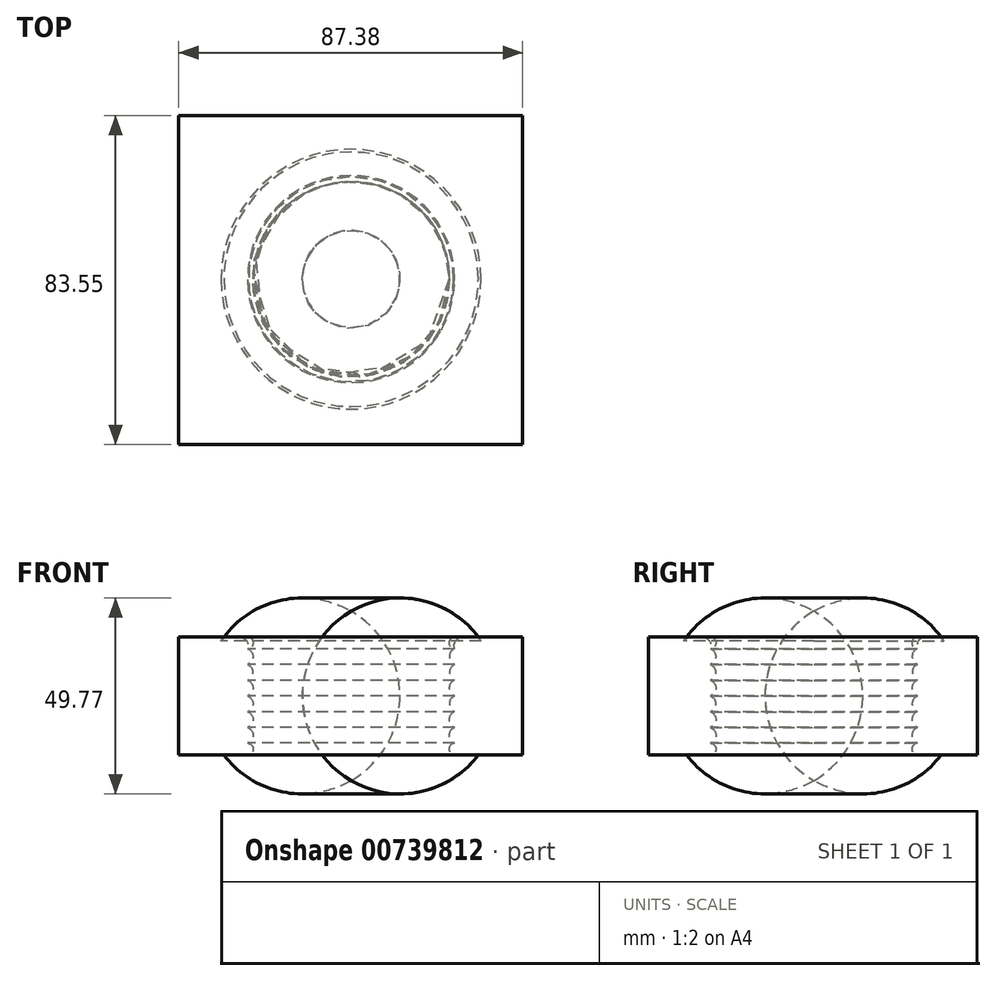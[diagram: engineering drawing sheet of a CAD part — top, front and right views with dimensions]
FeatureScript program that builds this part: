
annotation { "Feature Type Name" : "Feature", "Feature Type Description" : "" }
export const myFeature = defineFeature(function(context is Context, id is Id, definition is map)
    precondition{}
    {
        {
            var Q0;
            Q0=qCreatedBy(makeId("Top.planeOp"),FACE);
            cPlane(context, id + "F0", {"entities" : qUnion([Q0]), "cplaneType" : CPlaneType.OFFSET, "offset" : 30 * mm, "width" : 150 * mm, "height" : 150 * mm});
        }
        {
            var Q0;
            Q0=qCreatedBy(id+"F0.planeOp",FACE);
            var sketch = newSketch(context, id + "F1", { "sketchPlane" : qUnion([Q0])});
            skCircle(sketch, "E0", {"center": v(0, 0) * mm, "radius": 26 * mm});
            skCircle(sketch, "E1", {"center": v(0, 0) * mm, "radius": 32.5 * mm});
            skSolve(sketch);
        }
        {
            var Q0;
            Q0=qCreatedBy(makeId("Front.planeOp"),FACE);
            var sketch = newSketch(context, id + "F2", { "sketchPlane" : qUnion([Q0])});
            skArc(sketch, "E2", {"start": v(32.33, 0) * mm, "mid": v(37.35, 15) * mm, "end": v(32.32, 30) * mm});
            skLineSegment(sketch, "E3", {"start": v(12.47, 15) * mm, "end": v(50.15, 15) * mm, "construction": true});
            skLineSegment(sketch, "E4", {"start": v(12.47, 15) * mm, "end": v(12.47, 19) * mm, "construction": true});
            skLineSegment(sketch, "E5", {"start": v(12.47, 19) * mm, "end": v(49.8, 19) * mm, "construction": true});
            skLineSegment(sketch, "E6", {"start": v(49.8, 19) * mm, "end": v(49.8, 23) * mm, "construction": true});
            skLineSegment(sketch, "E7", {"start": v(49.8, 23) * mm, "end": v(12.47, 23) * mm, "construction": true});
            skLineSegment(sketch, "E8", {"start": v(12.47, 23) * mm, "end": v(12.47, 27) * mm, "construction": true});
            skLineSegment(sketch, "E9", {"start": v(12.47, 27) * mm, "end": v(49.98, 27) * mm, "construction": true});
            skLineSegment(sketch, "E10", {"start": v(49.98, 27) * mm, "end": v(49.98, 30) * mm, "construction": true});
            skLineSegment(sketch, "E11", {"start": v(50.15, 15) * mm, "end": v(50.15, 11) * mm, "construction": true});
            skLineSegment(sketch, "E12", {"start": v(50.15, 11) * mm, "end": v(12.79, 11) * mm, "construction": true});
            skLineSegment(sketch, "E13", {"start": v(12.79, 11) * mm, "end": v(12.79, 7) * mm, "construction": true});
            skLineSegment(sketch, "E14", {"start": v(12.79, 7) * mm, "end": v(50.15, 7) * mm, "construction": true});
            skLineSegment(sketch, "E15", {"start": v(50.15, 7) * mm, "end": v(50.15, 3) * mm, "construction": true});
            skLineSegment(sketch, "E16", {"start": v(50.15, 3) * mm, "end": v(13.06, 3) * mm, "construction": true});
            skLineSegment(sketch, "E17", {"start": v(13.06, 3) * mm, "end": v(13.06, 0) * mm, "construction": true});
            skLineSegment(sketch, "E18", {"start": v(13.06, 0) * mm, "end": v(50.15, 0) * mm, "construction": true});
            skArc(sketch, "E19", {"start": v(26, 29.95) * mm, "mid": v(24.87, 28.34) * mm, "end": v(26.32, 27) * mm});
            skArc(sketch, "E20", {"start": v(26.32, 27) * mm, "mid": v(24.95, 25) * mm, "end": v(26.32, 23) * mm});
            skArc(sketch, "E21", {"start": v(26.32, 23) * mm, "mid": v(24.99, 21) * mm, "end": v(26.32, 19) * mm});
            skArc(sketch, "E22", {"start": v(26.32, 19) * mm, "mid": v(24.91, 17) * mm, "end": v(26.32, 15) * mm});
            skArc(sketch, "E23", {"start": v(26.32, 15) * mm, "mid": v(24.95, 13) * mm, "end": v(26.32, 11) * mm});
            skArc(sketch, "E24", {"start": v(26.32, 11) * mm, "mid": v(24.9, 9) * mm, "end": v(26.32, 7) * mm});
            skArc(sketch, "E25", {"start": v(26.32, 7) * mm, "mid": v(24.9, 5) * mm, "end": v(26.32, 3) * mm});
            skArc(sketch, "E26", {"start": v(26.32, 3) * mm, "mid": v(24.9, 1.5) * mm, "end": v(26.32, 0) * mm});
            skLineSegment(sketch, "E27", {"start": v(26, 29.95) * mm, "end": v(32.32, 30) * mm});
            skLineSegment(sketch, "E28", {"start": v(26.32, 0) * mm, "end": v(32.33, 0) * mm});
            skLineSegment(sketch, "E29", {"start": v(25, 30.36) * mm, "end": v(24.9, -1.2) * mm, "construction": true});
            skPoint(sketch, "E29.endSnap0", {"position": v(24.9, 1.5) * mm});
            skSolve(sketch);
        }
        {
            var Q0;
            Q0=makeQuery(id+"F2.imprint","IMPRINT",FACE,{"disambiguationData":[TD([[makeQuery(id+"F2.imprint","IMPRINT",EDGE,{"derivedFrom":sQuery(id+"F2.wireOp",EDGE,"E2")}),1.0]])]});
            var Q1;
            Q1=sQuery(id+"F2.wireOp",EDGE,"E22");
            var Q2;
            Q2=sQuery(id+"F2.wireOp",EDGE,"E21");
            var Q3;
            Q3=sQuery(id+"F2.wireOp",EDGE,"E20");
            var Q4;
            Q4=sQuery(id+"F2.wireOp",EDGE,"E27");
            var Q5;
            Q5=sQuery(id+"F2.wireOp",EDGE,"E19");
            var Q6;
            Q6=sQuery(id+"F2.wireOp",EDGE,"E2");
            var Q7;
            Q7=sQuery(id+"F2.wireOp",EDGE,"E23");
            var Q8;
            Q8=sQuery(id+"F2.wireOp",EDGE,"E24");
            var Q9;
            Q9=sQuery(id+"F2.wireOp",EDGE,"E25");
            var Q10;
            Q10=sQuery(id+"F2.wireOp",EDGE,"E26");
            var Q11;
            Q11=sQuery(id+"F2.wireOp",EDGE,"E28");
            var Q12;
            Q12=sQuery(id+"F1.wireOp",EDGE,"E0");
            sweep(context, id + "F3", {"bodyType" : ExtendedToolBodyType.SURFACE, "profiles" : qUnion([Q0]), "surfaceProfiles" : qUnion([Q1, Q2, Q3, Q4, Q5, Q6, Q7, Q8, Q9, Q10, Q11]), "path" : qUnion([Q12])});
        }
        {
            var Q0;
            Q0=makeQuery(id+"F3.opSweep","SWEPT_FACE",FACE,{"disambiguationData":[OSD([sQuery(id+"F1.wireOp",EDGE,"E0"),sQuery(id+"F2.wireOp",EDGE,"E27")])]});
            fillet(context, id + "F4", {"entities" : qUnion([Q0]), "radius" : 2 * mm, "tangentPropagation" : true, "allowEdgeOverflow" : false});
        }
        {
            var Q0;
            Q0=qCreatedBy(id+"F0.planeOp",FACE);
            var sketch = newSketch(context, id + "F5", { "sketchPlane" : qUnion([Q0])});
            skLineSegment(sketch, "E30.bottom", {"start": v(-43.8, 41.56) * mm, "end": v(43.58, 41.56) * mm});
            skLineSegment(sketch, "E30.top", {"start": v(-43.8, -41.99) * mm, "end": v(43.58, -41.99) * mm});
            skLineSegment(sketch, "E30.left", {"start": v(-43.8, 41.56) * mm, "end": v(-43.8, -41.99) * mm});
            skLineSegment(sketch, "E30.right", {"start": v(43.58, 41.56) * mm, "end": v(43.58, -41.99) * mm});
            skSolve(sketch);
        }
        {
            var Q0;
            Q0=makeQuery(id+"F5.imprint","IMPRINT",FACE,{"disambiguationData":[TD([[makeQuery(id+"F5.imprint","IMPRINT",EDGE,{"derivedFrom":sQuery(id+"F5.wireOp",EDGE,"E30.bottom")}),-1.0]])]});
            extrude(context, id + "F6", {"entities" : qUnion([Q0]), "depth" : 0 * mm, "offsetDistance" : 25 * mm, "hasSecondDirection" : true, "secondDirectionOppositeDirection" : true, "secondDirectionDepth" : 30 * mm});
        }
        {
            var Q0;
            Q0=makeQuery(id+"F2.imprint","IMPRINT",FACE,{"disambiguationData":[TD([[makeQuery(id+"F2.imprint","IMPRINT",EDGE,{"derivedFrom":sQuery(id+"F2.wireOp",EDGE,"E2")}),1.0]])]});
            var Q1;
            Q1=sQuery(id+"F1.wireOp",EDGE,"E0");
            sweep(context, id + "F7", {"operationType" : NewBodyOperationType.REMOVE, "profiles" : qUnion([Q0]), "path" : qUnion([Q1])});
        }
        {
            var Q0;
            Q0=makeQuery(id+"F5.imprint","IMPRINT",FACE,{"disambiguationData":[TD([[makeQuery(id+"F5.imprint","IMPRINT",EDGE,{"derivedFrom":sQuery(id+"F5.wireOp",EDGE,"E30.bottom")}),-1.0]])]});
            extrude(context, id + "F8", {"entities" : qUnion([Q0]), "oppositeDirection" : true, "depth" : 30 * mm, "offsetDistance" : 25 * mm});
        }
        {
            var Q0;
            Q0=makeQuery(id+"F6.opExtrude","SWEPT_BODY",BODY,{"disambiguationData":[OSD([sQuery(id+"F5.wireOp",EDGE,"E30.bottom"),sQuery(id+"F5.wireOp",EDGE,"E30.top"),sQuery(id+"F5.wireOp",EDGE,"E30.left"),sQuery(id+"F5.wireOp",EDGE,"E30.right")])]});
            var Q1;
            Q1=makeQuery(id+"F8.opExtrude","SWEPT_BODY",BODY,{"disambiguationData":[OSD([sQuery(id+"F5.wireOp",EDGE,"E30.bottom"),sQuery(id+"F5.wireOp",EDGE,"E30.top"),sQuery(id+"F5.wireOp",EDGE,"E30.left"),sQuery(id+"F5.wireOp",EDGE,"E30.right")])]});
            booleanBodies(context, id + "F9", {"operationType" : BooleanOperationType.SUBTRACTION, "tools" : qUnion([Q0]), "targets" : qUnion([Q1]), "keepTools" : true});
        }
        {
            var Q0;
            Q0=makeQuery(id+"F9.opBoolean","COPY",FACE,{"derivedFrom":makeQuery(id+"F7.boolean.opBoolean","COPY",FACE,{"derivedFrom":makeQuery(id+"F7.opSweep","SWEPT_FACE",FACE,{"disambiguationData":[OSD([sQuery(id+"F1.wireOp",EDGE,"E0"),sQuery(id+"F2.wireOp",EDGE,"E27")])]})})});
            fillet(context, id + "F10", {"entities" : qUnion([Q0]), "radius" : 2.2 * mm, "tangentPropagation" : true, "allowEdgeOverflow" : false});
        }
    });
